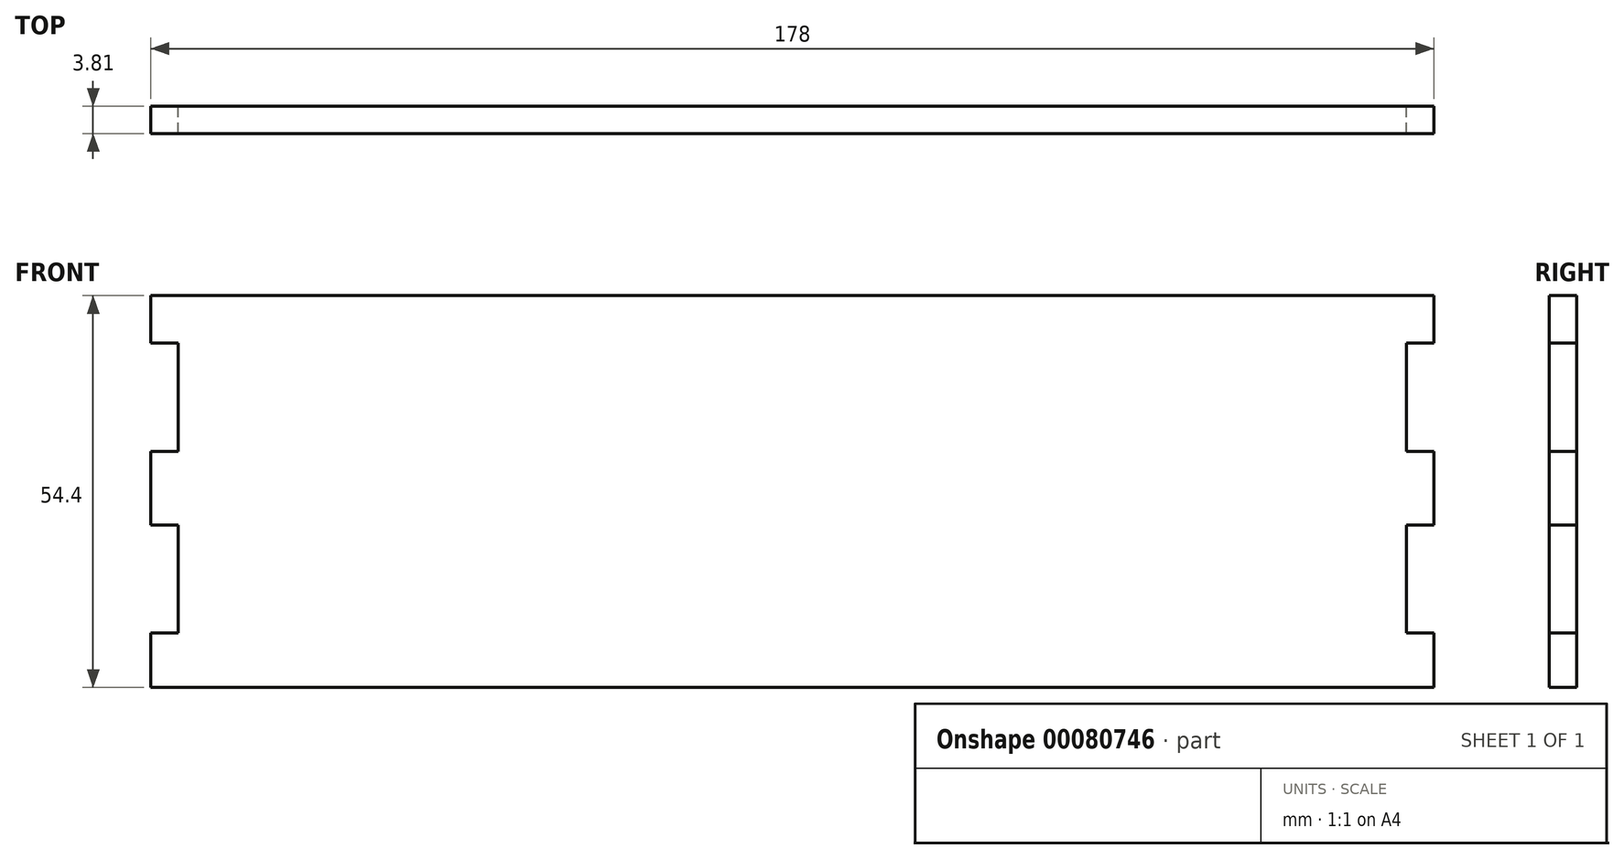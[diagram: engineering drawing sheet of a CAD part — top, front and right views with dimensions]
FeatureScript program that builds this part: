
annotation { "Feature Type Name" : "Feature", "Feature Type Description" : "" }
export const myFeature = defineFeature(function(context is Context, id is Id, definition is map)
    precondition{}
    {
        {
            var Q0;
            Q0=qCreatedBy(makeId("Front.planeOp"),FACE);
            var sketch = newSketch(context, id + "F0", { "sketchPlane" : qUnion([Q0])});
            skLineSegment(sketch, "E0.bottom", {"start": v(89, 27.2) * mm, "end": v(-89, 27.2) * mm});
            skLineSegment(sketch, "E0.top", {"start": v(89, -27.2) * mm, "end": v(-89, -27.2) * mm});
            skLineSegment(sketch, "E0.left", {"start": v(89, 27.2) * mm, "end": v(89, -27.2) * mm});
            skLineSegment(sketch, "E0.right", {"start": v(-89, 27.2) * mm, "end": v(-89, -27.2) * mm});
            skPoint(sketch, "E0.middle", {"position": v(0, 0) * mm});
            skLineSegment(sketch, "E1", {"start": v(0, 27.2) * mm, "end": v(0, -27.2) * mm});
            skLineSegment(sketch, "E2", {"start": v(-89, 0) * mm, "end": v(89, 0) * mm});
            skLineSegment(sketch, "E3.MirrorCS", {"start": v(82.18, 31.01) * mm, "end": v(64, 31.01) * mm});
            skLineSegment(sketch, "E4", {"start": v(64, 31.01) * mm, "end": v(64, 27.2) * mm});
            skLineSegment(sketch, "E5", {"start": v(82.18, 31.01) * mm, "end": v(82.18, 27.2) * mm});
            skLineSegment(sketch, "E6.MirrorCS", {"start": v(82.18, -31.01) * mm, "end": v(64, -31.01) * mm});
            skLineSegment(sketch, "E7.MirrorCS", {"start": v(64, -31.01) * mm, "end": v(64, -27.2) * mm});
            skLineSegment(sketch, "E8.MirrorCS", {"start": v(82.18, -31.01) * mm, "end": v(82.18, -27.2) * mm});
            skLineSegment(sketch, "E9.MirrorCS", {"start": v(-82.18, 31.01) * mm, "end": v(-64, 31.01) * mm});
            skLineSegment(sketch, "E10.MirrorCS", {"start": v(-64, 31.01) * mm, "end": v(-64, 27.2) * mm});
            skLineSegment(sketch, "E11.MirrorCS", {"start": v(-82.18, 31.01) * mm, "end": v(-82.18, 27.2) * mm});
            skLineSegment(sketch, "E12.MirrorCS", {"start": v(-64, -31.01) * mm, "end": v(-64, -27.2) * mm});
            skLineSegment(sketch, "E13.MirrorCS", {"start": v(-82.18, -31.01) * mm, "end": v(-64, -31.01) * mm});
            skLineSegment(sketch, "E14.MirrorCS", {"start": v(-82.18, -31.01) * mm, "end": v(-82.18, -27.2) * mm});
            skLineSegment(sketch, "E15", {"start": v(-54, 27.2) * mm, "end": v(-54, 31.01) * mm});
            skLineSegment(sketch, "E16", {"start": v(-54, 31.01) * mm, "end": v(-39, 31.01) * mm});
            skLineSegment(sketch, "E17", {"start": v(-39, 31.01) * mm, "end": v(-39, 27.2) * mm});
            skLineSegment(sketch, "E18.MirrorCS", {"start": v(-54, -31.01) * mm, "end": v(-39, -31.01) * mm});
            skLineSegment(sketch, "E19.MirrorCS", {"start": v(-54, -27.2) * mm, "end": v(-54, -31.01) * mm});
            skLineSegment(sketch, "E20.MirrorCS", {"start": v(-39, -31.01) * mm, "end": v(-39, -27.2) * mm});
            skLineSegment(sketch, "E21.MirrorCS", {"start": v(54, 31.01) * mm, "end": v(39, 31.01) * mm});
            skLineSegment(sketch, "E22.MirrorCS", {"start": v(39, 31.01) * mm, "end": v(39, 27.2) * mm});
            skLineSegment(sketch, "E23.MirrorCS", {"start": v(54, 27.2) * mm, "end": v(54, 31.01) * mm});
            skLineSegment(sketch, "E24.MirrorCS", {"start": v(54, -31.01) * mm, "end": v(39, -31.01) * mm});
            skLineSegment(sketch, "E25.MirrorCS", {"start": v(54, -27.2) * mm, "end": v(54, -31.01) * mm});
            skLineSegment(sketch, "E26.MirrorCS", {"start": v(39, -31.01) * mm, "end": v(39, -27.2) * mm});
            skLineSegment(sketch, "E27", {"start": v(-89, 20.6) * mm, "end": v(-85.19, 20.6) * mm});
            skLineSegment(sketch, "E28", {"start": v(-85.19, 20.6) * mm, "end": v(-85.19, 5.6) * mm});
            skLineSegment(sketch, "E29", {"start": v(-85.19, 5.6) * mm, "end": v(-89, 5.6) * mm});
            skLineSegment(sketch, "E30", {"start": v(-89, -4.63) * mm, "end": v(-85.19, -4.63) * mm});
            skLineSegment(sketch, "E31", {"start": v(-85.19, -4.63) * mm, "end": v(-85.19, -19.63) * mm});
            skLineSegment(sketch, "E32", {"start": v(-85.19, -19.63) * mm, "end": v(-89, -19.63) * mm});
            skLineSegment(sketch, "E33.MirrorCS", {"start": v(85.19, 20.6) * mm, "end": v(85.19, 5.6) * mm});
            skLineSegment(sketch, "E34.MirrorCS", {"start": v(89, 20.6) * mm, "end": v(85.19, 20.6) * mm});
            skLineSegment(sketch, "E35.MirrorCS", {"start": v(85.19, 5.6) * mm, "end": v(89, 5.6) * mm});
            skLineSegment(sketch, "E36.MirrorCS", {"start": v(89, -4.63) * mm, "end": v(85.19, -4.63) * mm});
            skLineSegment(sketch, "E37.MirrorCS", {"start": v(85.19, -4.63) * mm, "end": v(85.19, -19.63) * mm});
            skLineSegment(sketch, "E38.MirrorCS", {"start": v(85.19, -19.63) * mm, "end": v(89, -19.63) * mm});
            skSolve(sketch);
        }
        {
            var Q0;
            Q0=makeQuery(id+"F0.imprint","IMPRINT",FACE,{"disambiguationData":[TD([[makeQuery(id+"F0.imprint","IMPRINT",EDGE,{"derivedFrom":sQuery(id+"F0.wireOp",EDGE,"E0.bottom")}),1.0]])]});
            var Q1;
            {var subQ0=sQuery(id+"F0.wireOp",EDGE,"fd9a9881-1114-4a34-881d-6aab33066d9a0.MirrorCS");Q1=makeQuery(id+"F0.imprint","IMPRINT",FACE,{"disambiguationData":[TD([[makeQuery(id+"F0.imprint","IMPRINT",EDGE,{"derivedFrom":subQ0}),-1.0]])]});}
            var Q2;
            Q2=makeQuery(id+"F0.imprint","IMPRINT",FACE,{"disambiguationData":[TD([[makeQuery(id+"F0.imprint","IMPRINT",EDGE,{"derivedFrom":sQuery(id+"F0.wireOp",EDGE,"e9cbb39e-25d4-43ef-8b23-404016609ed90.MirrorCS")}),1.0]])]});
            var Q3;
            {var subQ0=sQuery(id+"F0.wireOp",EDGE,"E0.top");var subQ9=sQuery(id+"F0.wireOp",EDGE,"E1");var subQ10=makeQuery(id+"F0.imprint","INTERSECT",VERTEX,{"derivedFrom":[subQ0,subQ9]});Q3=makeQuery(id+"F0.imprint","IMPRINT",FACE,{"disambiguationData":[TD([[makeQuery(id+"F0.imprint","IMPRINT",EDGE,{"disambiguationData":[TD([[subQ10,-1.0]])],"derivedFrom":subQ0}),-1.0]])]});}
            var Q4;
            {var subQ0=sQuery(id+"F0.wireOp",EDGE,"E0.top");var subQ5=sQuery(id+"F0.wireOp",EDGE,"E0.left");var subQ6=makeQuery(id+"F0.imprint","INTERSECT",VERTEX,{"derivedFrom":[subQ0,subQ5]});Q4=makeQuery(id+"F0.imprint","IMPRINT",FACE,{"disambiguationData":[TD([[makeQuery(id+"F0.imprint","IMPRINT",EDGE,{"disambiguationData":[TD([[subQ6,-1.0]])],"derivedFrom":subQ0}),-1.0]])]});}
            var Q5;
            {var subQ0=sQuery(id+"F0.wireOp",EDGE,"401eab21-d0eb-4b6a-999c-0202608270cc0.MirrorCS");Q5=makeQuery(id+"F0.imprint","IMPRINT",FACE,{"disambiguationData":[TD([[makeQuery(id+"F0.imprint","IMPRINT",EDGE,{"derivedFrom":subQ0}),-1.0]])]});}
            var Q6;
            Q6=makeQuery(id+"F0.imprint","IMPRINT",FACE,{"disambiguationData":[TD([[makeQuery(id+"F0.imprint","IMPRINT",EDGE,{"derivedFrom":sQuery(id+"F0.wireOp",EDGE,"30391e0d-861b-499c-bc64-7791a20e464f0.MirrorCS")}),-1.0]])]});
            var Q7;
            {var subQ0=sQuery(id+"F0.wireOp",EDGE,"6473a4aa-d753-4074-8c14-d968af5e0e340.MirrorCS");Q7=makeQuery(id+"F0.imprint","IMPRINT",FACE,{"disambiguationData":[TD([[makeQuery(id+"F0.imprint","IMPRINT",EDGE,{"derivedFrom":subQ0}),-1.0]])]});}
            var Q8;
            Q8=makeQuery(id+"F0.imprint","IMPRINT",FACE,{"disambiguationData":[TD([[makeQuery(id+"F0.imprint","IMPRINT",EDGE,{"derivedFrom":sQuery(id+"F0.wireOp",EDGE,"fecd9772-fa22-4386-91d1-5c1f6a4e36900.MirrorCS")}),1.0]])]});
            var Q9;
            Q9=makeQuery(id+"F0.imprint","IMPRINT",FACE,{"disambiguationData":[TD([[makeQuery(id+"F0.imprint","IMPRINT",EDGE,{"derivedFrom":sQuery(id+"F0.wireOp",EDGE,"5e35dc9c-8b32-406b-8670-51bc3dacd16a0.MirrorCS")}),-1.0]])]});
            var Q10;
            Q10=makeQuery(id+"F0.imprint","IMPRINT",FACE,{"disambiguationData":[TD([[makeQuery(id+"F0.imprint","IMPRINT",EDGE,{"derivedFrom":sQuery(id+"F0.wireOp",EDGE,"d01f1c85-b5f6-4cd6-8d75-d1ca25df48720.MirrorCS")}),-1.0]])]});
            var Q11;
            {var subQ0=sQuery(id+"F0.wireOp",EDGE,"64aee7ef-a2d6-4a05-a809-71a0f63b7b4d0.MirrorCS");Q11=makeQuery(id+"F0.imprint","IMPRINT",FACE,{"disambiguationData":[TD([[makeQuery(id+"F0.imprint","IMPRINT",EDGE,{"derivedFrom":subQ0}),-1.0]])]});}
            var Q12;
            Q12=makeQuery(id+"F0.imprint","IMPRINT",FACE,{"disambiguationData":[TD([[makeQuery(id+"F0.imprint","IMPRINT",EDGE,{"derivedFrom":sQuery(id+"F0.wireOp",EDGE,"5e85ca08-a0c1-4344-8977-c1e94523da100.MirrorCS")}),1.0]])]});
            var Q13;
            Q13=makeQuery(id+"F0.imprint","IMPRINT",FACE,{"disambiguationData":[TD([[makeQuery(id+"F0.imprint","IMPRINT",EDGE,{"derivedFrom":sQuery(id+"F0.wireOp",EDGE,"6f26e7cf-d43b-4aba-8b23-2f0c2296f61f0.MirrorCS")}),1.0]])]});
            var Q14;
            Q14=makeQuery(id+"F0.imprint","IMPRINT",FACE,{"disambiguationData":[TD([[makeQuery(id+"F0.imprint","IMPRINT",EDGE,{"derivedFrom":sQuery(id+"F0.wireOp",EDGE,"71418182-0ad3-425f-ac6c-b0ad9801f65d0.MirrorCS")}),1.0]])]});
            var Q15;
            Q15=makeQuery(id+"F0.imprint","IMPRINT",FACE,{"disambiguationData":[TD([[makeQuery(id+"F0.imprint","IMPRINT",EDGE,{"derivedFrom":sQuery(id+"F0.wireOp",EDGE,"0c83b9c4-936b-4906-90ef-ea555f0fafea0.MirrorCS")}),-1.0]])]});
            var Q16;
            {var subQ7=sQuery(id+"F0.wireOp",EDGE,"E27");Q16=makeQuery(id+"F0.imprint","IMPRINT",FACE,{"disambiguationData":[TD([[makeQuery(id+"F0.imprint","IMPRINT",EDGE,{"derivedFrom":subQ7}),1.0]])]});}
            extrude(context, id + "F1", {"entities" : qUnion([Q0, Q1, Q2, Q3, Q4, Q5, Q6, Q7, Q8, Q9, Q10, Q11, Q12, Q13, Q14, Q15, Q16]), "depth" : 3.8 * mm});
        }
    });
